AUTODESK INVENTOR PART (.ipt)
format: ipt  version: 2018 (Build 220112000, 112)  size: 181,248 bytes
history: native  units: mm
features: sketch x4, fillet x4, extrude x3
ambient origin geometry x8: Origin, YZ Plane, XZ Plane, XY Plane, X Axis, Y Axis, Z Axis, Center Point
bodies: Solid1 (feature_tree)
feature tree (11):
  sketch  "Sketch1"  dims[d0=15.0mm d1=55.0mm]
  extrude  "Extrusion1"  Depth=55.0mm
  extrude  "Extrusion2"  Depth=3.5mm
  extrude  "Extrusion3"  Depth=3.0mm TaperAngle=0.0deg
  fillet  "Fillet1"  Radius=10.856158mm
  fillet  "Fillet2"  Radius=17.0mm
  fillet  "Fillet3"  Radius=12.0mm
  fillet  "Fillet4"  Radius=3.0mm
  sketch  "Sketch2"  dims[d2=3.0mm d3=0.0mm d4=3.5mm]
  sketch  "Sketch3"  dims[d5=45.153mm d6=3.0mm d7=0.0mm d10=10.856158mm d11=17.0mm d12=12.0mm d13=3.0mm]
  sketch  "Sketch4"  dims[d14=3.0mm d15=0.0mm d16=3.0mm d17=2.0mm d18=5.0mm d19=2.0mm]
